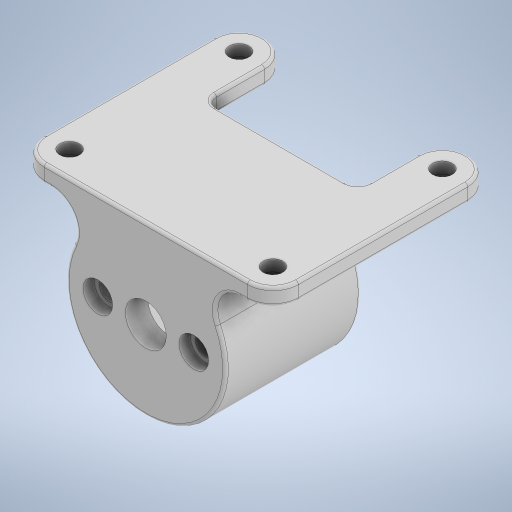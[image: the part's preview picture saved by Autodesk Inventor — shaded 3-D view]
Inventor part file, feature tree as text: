
AUTODESK INVENTOR PART (.ipt)
format: ipt  version: 2024.2 (Build 282272000, 272)  size: 438,272 bytes
history: native  units: mm
features: extrude x6, sketch x6, fillet x3, plane x1
ambient origin geometry x8: Origin, YZ Plane, XZ Plane, XY Plane, X Axis, Y Axis, Z Axis, Center Point
bodies: Solid1 (feature_tree)
feature tree (16):
  extrude  "Extrusion1"  Depth=3.5mm
  extrude  "Extrusion2"  Depth=28.2mm
  plane  "Work Plane1"
  extrude  "Extrusion6"  Depth=4.0mm
  extrude  "Extrusion7"  Depth=12.6mm
  fillet  "Fillet3"  Radius=45.0mm
  extrude  "Extrusion8"  Depth=4.5mm
  fillet  "Fillet4"  Radius=4.5mm
  fillet  "Fillet5"  Radius=4.5mm
  extrude  "Extrusion5"  Depth=0.5mm
  sketch  "Sketch1"  dims[d0=7.25mm d1=3.5mm]
  sketch  "Sketch2"  dims[d2=17.0mm d3=28.2mm]
  sketch  "Sketch3"  dims[d4=4.0mm d5=0.0mm d6=25.2mm]
  sketch  "Sketch5"  dims[d7=20.0mm d8=0.0mm d13=12.6mm d14=45.0mm]
  sketch  "Sketch6"  dims[d15=22.5mm d16=3.5mm d17=4.5mm d18=4.5mm]
  sketch  "Sketch7"  dims[d19=4.5mm d28=5.25mm d29=2.0mm d30=0.0mm d31=30.0mm d44=3.0mm d45=0.0mm d46=5.25mm d47=1.0mm d48=0.0mm d49=4.5mm d50=1.0mm d51=0.0mm d52=2.0mm d53=0.5mm d42=0.5mm d43=0.872665mm]
